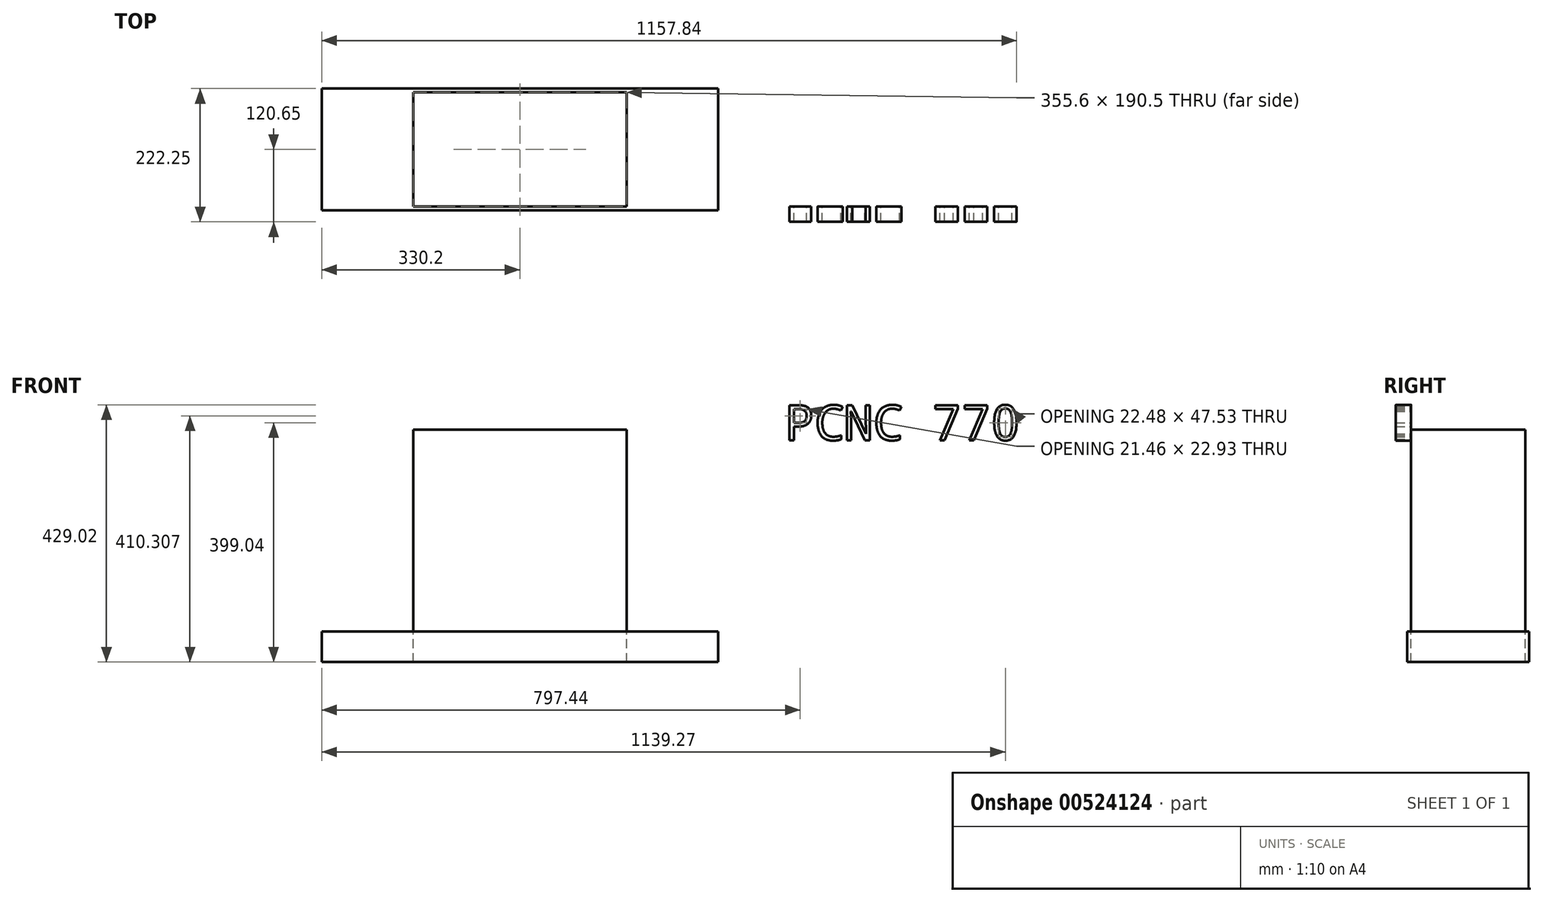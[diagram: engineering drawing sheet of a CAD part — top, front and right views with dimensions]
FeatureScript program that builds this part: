
annotation { "Feature Type Name" : "Feature", "Feature Type Description" : "" }
export const myFeature = defineFeature(function(context is Context, id is Id, definition is map)
    precondition{}
    {
        {
            var Q0;
            Q0=qCreatedBy(makeId("Front.planeOp"),FACE);
            cPlane(context, id + "F0", {"entities" : qUnion([Q0]), "cplaneType" : CPlaneType.OFFSET, "offset" : 149.88 * mm, "width" : 152.4 * mm, "height" : 152.4 * mm});
        }
        {
            var Q0;
            Q0=qCreatedBy(id+"F0.planeOp",FACE);
            var sketch = newSketch(context, id + "F1", { "sketchPlane" : qUnion([Q0])});
            skCircle(sketch, "E0", {"center": v(36.84, -33.98) * mm, "radius": 26.82 * mm});
            skSolve(sketch);
        }
        {
            var Q0;
            Q0=qCreatedBy(makeId("Front.planeOp"),FACE);
            var sketch = newSketch(context, id + "F2", { "sketchPlane" : qUnion([Q0])});
            skCircle(sketch, "E1", {"center": v(0, 0) * mm, "radius": 57.3 * mm});
            skSolve(sketch);
        }
        {
            var Q0;
            Q0=makeQuery(id+"F2.imprint","IMPRINT",FACE,{"disambiguationData":[TD([[makeQuery(id+"F2.imprint","IMPRINT",EDGE,{"derivedFrom":sQuery(id+"F2.wireOp",EDGE,"E1")}),1.0]])]});
            var Q1;
            Q1=makeQuery(id+"F1.imprint","IMPRINT",FACE,{"disambiguationData":[TD([[makeQuery(id+"F1.imprint","IMPRINT",EDGE,{"derivedFrom":sQuery(id+"F1.wireOp",EDGE,"E0")}),1.0]])]});
            var Q2;
            Q2=makeQuery(id+"F2.imprint","IMPRINT",FACE,{"disambiguationData":[TD([[makeQuery(id+"F2.imprint","IMPRINT",EDGE,{"derivedFrom":sQuery(id+"F2.wireOp",EDGE,"E1")}),1.0]])]});
            var Q3;
            Q3=makeQuery(id+"F1.imprint","IMPRINT",FACE,{"disambiguationData":[TD([[makeQuery(id+"F1.imprint","IMPRINT",EDGE,{"derivedFrom":sQuery(id+"F1.wireOp",EDGE,"E0")}),1.0]])]});
            loft(context, id + "F3", {"bodyType" : ToolBodyType.SURFACE, "sheetProfilesArray" : [{ "sheetProfileEntities" : qUnion([Q0]) }, { "sheetProfileEntities" : qUnion([Q1]) }], "wireProfilesArray" : [{ "wireProfileEntities" : qUnion([Q2]) }, { "wireProfileEntities" : qUnion([Q3]) }]});
        }
        {
            var Q0;
            Q0=qCreatedBy(makeId("Top.planeOp"),FACE);
            var sketch = newSketch(context, id + "F4", { "sketchPlane" : qUnion([Q0])});
            skLineSegment(sketch, "E2.bottom", {"start": v(330.2, -101.6) * mm, "end": v(-330.2, -101.6) * mm});
            skLineSegment(sketch, "E2.top", {"start": v(330.2, 101.6) * mm, "end": v(-330.2, 101.6) * mm});
            skLineSegment(sketch, "E2.left", {"start": v(330.2, -101.6) * mm, "end": v(330.2, 101.6) * mm});
            skLineSegment(sketch, "E2.right", {"start": v(-330.2, -101.6) * mm, "end": v(-330.2, 101.6) * mm});
            skPoint(sketch, "E2.middle", {"position": v(0, 0) * mm});
            skLineSegment(sketch, "E3.bottom", {"start": v(177.8, -95.25) * mm, "end": v(-177.8, -95.25) * mm});
            skLineSegment(sketch, "E3.top", {"start": v(177.8, 95.25) * mm, "end": v(-177.8, 95.25) * mm});
            skLineSegment(sketch, "E3.left", {"start": v(177.8, -95.25) * mm, "end": v(177.8, 95.25) * mm});
            skLineSegment(sketch, "E3.right", {"start": v(-177.8, -95.25) * mm, "end": v(-177.8, 95.25) * mm});
            skSolve(sketch);
        }
        {
            var Q0;
            Q0 = qSketchRegion(id + "F4", true);
            extrude(context, id + "F5", {"entities" : qUnion([Q0]), "oppositeDirection" : true, "depth" : 50.8 * mm, "offsetDistance" : 25.4 * mm});
        }
        {
            var Q0;
            Q0=makeQuery(id+"F4.imprint","IMPRINT",FACE,{"disambiguationData":[TD([[makeQuery(id+"F4.imprint","IMPRINT",EDGE,{"derivedFrom":sQuery(id+"F4.wireOp",EDGE,"E3.bottom")}),-1.0]])]});
            extrude(context, id + "F6", {"entities" : qUnion([Q0]), "depth" : 336.55 * mm, "offsetDistance" : 25.4 * mm});
        }
        {
            var Q0;
            Q0=makeQuery(id+"F6.opExtrude","SWEPT_FACE",FACE,{"disambiguationData":[OSD([sQuery(id+"F4.wireOp",EDGE,"E3.bottom")])]});
            var sketch = newSketch(context, id + "F7", { "sketchPlane" : qUnion([Q0])});
            skText(sketch, "E4", { "text": "PCNC 770", "fontName": "DroidSansMono.ttf"});
            const initialGuessF7  = {"E4": [0.4421, 0.3191, 1, 0, 0.0587]};
            skSetInitialGuess(sketch, initialGuessF7);
            skSolve(sketch);
        }
        {
            var Q0;
            Q0 = qSketchRegion(id + "F7", true);
            extrude(context, id + "F8", {"entities" : qUnion([Q0]), "depth" : 25.4 * mm, "offsetDistance" : 25.4 * mm});
        }
    });
